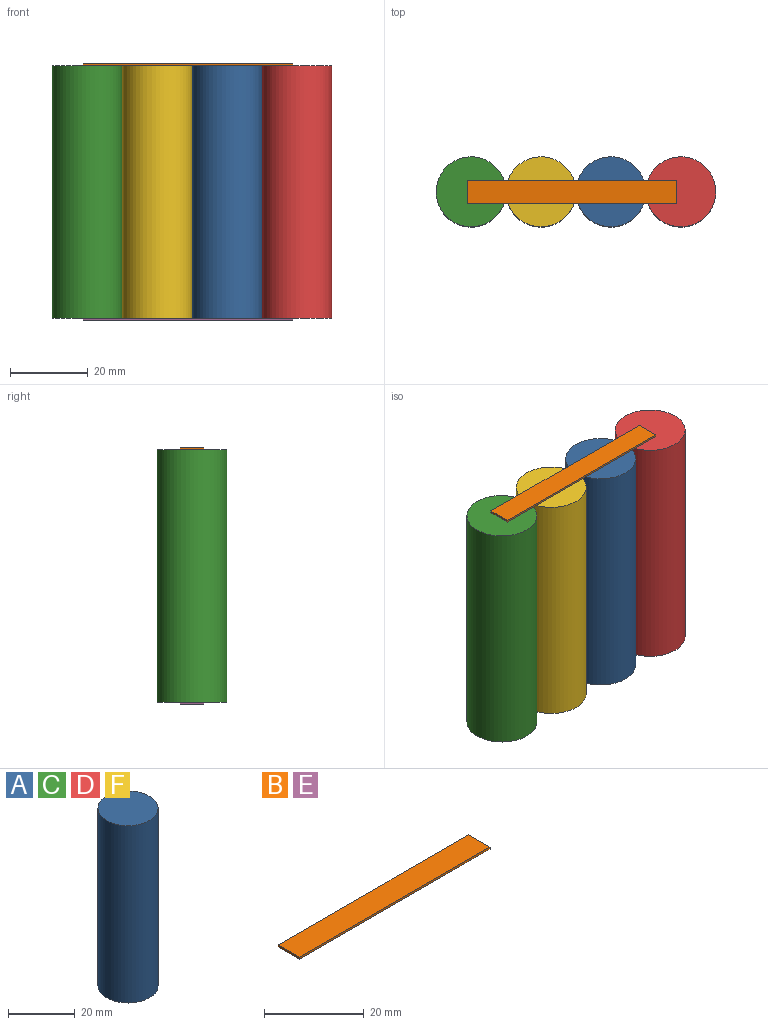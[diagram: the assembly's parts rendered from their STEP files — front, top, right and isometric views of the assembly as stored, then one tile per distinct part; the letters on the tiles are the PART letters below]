
ASSEMBLY  parts=6 mates=5
PART A: 3 faces, bbox 18x18x65 mm
  f0: cylinder r=9mm len=65mm, axis (0,0,-1), area 3675.7mm2, adj f1,f2
  f1: plane 18x18mm, normal (0,0,1), area 254.5mm2, adj f0
  f2: plane 18x18mm, normal (0,0,-1), area 254.5mm2, adj f0
PART B: 6 faces, bbox 54x6x0.5 mm
  f0: plane 6x0.5mm, normal (-1,0,0), area 3mm2, adj f1,f3,f4,f5
  f1: plane 54x0.5mm, normal (0,-1,0), area 27mm2, adj f0,f2,f4,f5
  f2: plane 6x0.5mm, normal (1,0,0), area 3mm2, adj f1,f3,f4,f5
  f3: plane 54x0.5mm, normal (0,1,0), area 27mm2, adj f0,f2,f4,f5
  f4: plane 54x6mm, normal (0,0,1), area 324mm2, adj f0,f1,f2,f3
  f5: plane 54x6mm, normal (0,0,-1), area 324mm2, adj f0,f1,f2,f3
PART C: same geometry as A
PART D: same geometry as A
PART E: same geometry as B
PART F: same geometry as A
PLACE A t=(-19.18,-6.65,84.67)mm
PLACE B t=(-56.18,-3.65,149.67)mm
PLACE C t=(-55.18,-6.65,84.67)mm
PLACE D t=(-1.18,-6.65,84.67)mm
PLACE E t=(-56.18,-3.65,84.17)mm
PLACE F t=(-37.18,-6.65,84.67)mm
MATE planar B.f3 <-> E.f3  axis (0,1,0) through (-29.18,-3.65,149.92)mm
MATE planar C.f0 <-> B.f5  axis (0,0,1) through (-55.18,-6.65,149.67)mm
MATE fastened B.f5 <-> D.f1  axis (0,0,-1) through (-29.18,-6.65,149.67)mm
MATE planar E.f2 <-> B.f2  axis (1,0,0) through (-2.18,-6.65,84.42)mm
MATE planar E.f4 <-> C.f0  axis (0,0,1) through (-29.18,-6.65,84.67)mm
